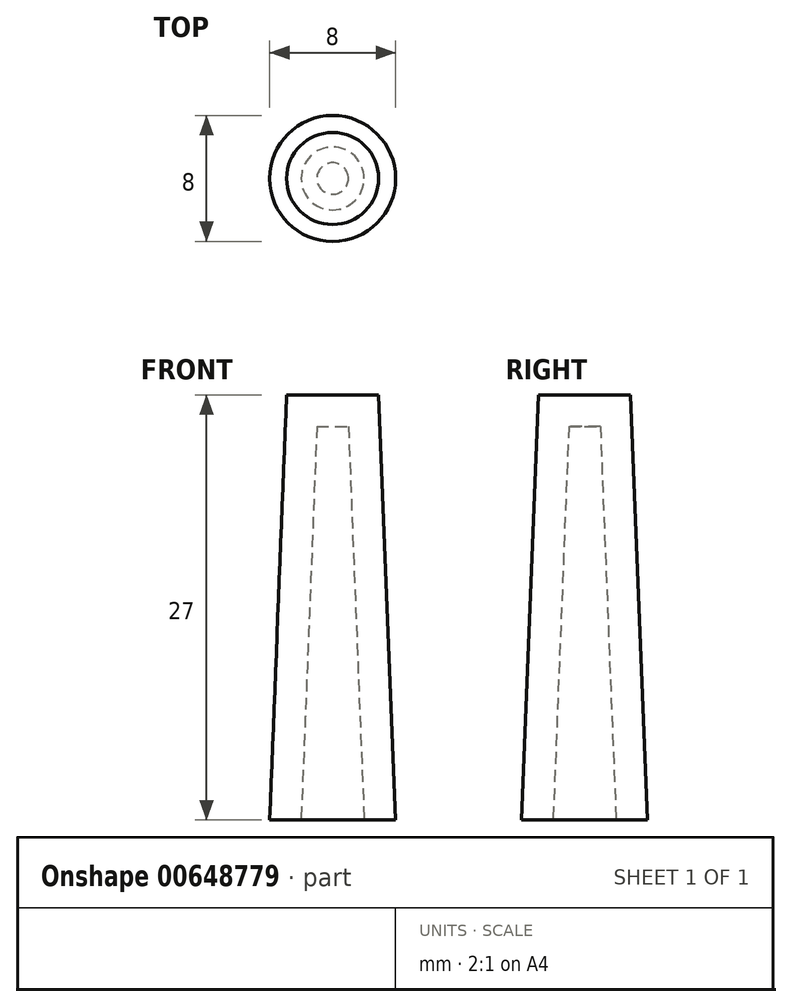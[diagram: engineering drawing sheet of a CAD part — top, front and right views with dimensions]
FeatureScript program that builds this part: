
annotation { "Feature Type Name" : "Feature", "Feature Type Description" : "" }
export const myFeature = defineFeature(function(context is Context, id is Id, definition is map)
    precondition{}
    {
        {
            var Q0;
            Q0=qCreatedBy(makeId("Front.planeOp"),FACE);
            var sketch = newSketch(context, id + "F0", { "sketchPlane" : qUnion([Q0])});
            skLineSegment(sketch, "E0", {"start": v(-26.71, 10.08) * mm, "end": v(-24.7, 10.08) * mm});
            skLineSegment(sketch, "E1", {"start": v(-22.7, 35.08) * mm, "end": v(-21.7, 35.08) * mm});
            skPoint(sketch, "E2.startSnap0", {"position": v(-22.7, 10.08) * mm});
            skLineSegment(sketch, "E3", {"start": v(-23.7, 35.08) * mm, "end": v(-24.7, 10.08) * mm});
            skLineSegment(sketch, "E4", {"start": v(-21.7, 35.08) * mm, "end": v(-20.7, 10.08) * mm});
            skPoint(sketch, "E2.end.orphan", {"position": v(-22.7, 10.08) * mm});
            skPoint(sketch, "E2.start.orphan", {"position": v(-22.7, -1) * mm});
            skLineSegment(sketch, "E5.0", {"start": v(-25.63, 37.08) * mm, "end": v(-26.71, 10.08) * mm});
            skLineSegment(sketch, "E5.1", {"start": v(-22.7, 37.08) * mm, "end": v(-19.79, 37.08) * mm});
            skLineSegment(sketch, "E5.2", {"start": v(-19.79, 37.08) * mm, "end": v(-18.7, 10.08) * mm});
            skLineSegment(sketch, "E6.trimOffspring", {"start": v(-20.7, 10.08) * mm, "end": v(-18.7, 10.08) * mm});
            skLineSegment(sketch, "E7", {"start": v(-22.7, 1.87) * mm, "end": v(-22.7, 10.08) * mm});
            skLineSegment(sketch, "E8.trimOffspring", {"start": v(-22.7, 35.08) * mm, "end": v(-22.7, 37.08) * mm});
            skSolve(sketch);
        }
        {
            var Q0;
            Q0 = qSketchRegion(id + "F0", true);
            var Q1;
            Q1=sQuery(id+"F0.wireOp",EDGE,"E7");
            revolve(context, id + "F1", {"entities" : qUnion([Q0]), "axis" : qUnion([Q1]), "revolveType" : RevolveType.FULL});
        }
    });
